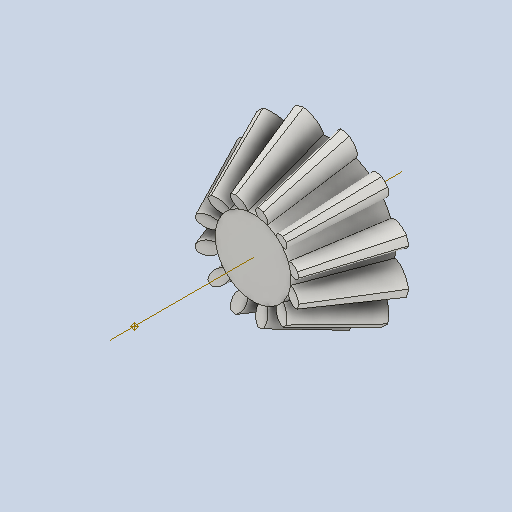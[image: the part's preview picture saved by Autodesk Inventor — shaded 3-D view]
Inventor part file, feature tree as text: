
AUTODESK INVENTOR PART (.ipt)
format: ipt  version: 2022 (Build 260153000, 153)  size: 490,496 bytes
history: native  units: mm
features: other x24, loft x2, pattern_circular x2, sketch x1
ambient origin geometry x6: Origin, XZ Plane, X Axis, Y Axis, Z Axis, Center Point
bodies: Solid1 (feature_tree)
feature tree (29):
  other  "Top Point"
  other  "Mesh Plane2"
  other  "Teeth Body"
  other  "Start Point"
  other  "Tooth Plane"
  other  "Start Sketch"
  other  "End Point"
  other  "3D Sketch Right"
  other  "End Plane Right"
  loft  "Loft Right"
  pattern_circular  "Circular Pattern Right"  [2 undecoded]
  other  "3D Sketch Left"
  other  "End Plane Left"
  loft  "Loft Left"
  pattern_circular  "Circular Pattern Left"  [2 undecoded]
  other  "Fix Body"
  other  "Mesh Plane"
  other  "Top Plane"
  other  "Teeth Body Sketch"
  other  "End Plane"
  other  "End Sketch"
  other  "Helical Curve Left"
  other  "End Sketch Left"
  other  "Body Sketch"
  sketch  "Sketch6"  dims[d0=24.0mm d1=19.543312mm d2=27.411178mm d3=12.9mm d4=29.317764mm d5=90.0deg d7=3.763947mm d8=5.032168mm d9=11.359554mm d11=13.111849mm d12=2.236532mm d15=2.990106mm d16=6.749829mm d17=0.0mm d18=90.0deg d19=0.0mm d20=90.0deg d21=120.0mm d22=360.0deg d26=153.94342mm d27=12.174046mm d28=24.0mm d29=-3.805064mm d30=2.236532mm d31=2.990106mm d32=6.749829mm d35=0.0mm d37=0.0mm d39=0.0mm d40=90.0deg d41=120.0mm d42=360.0deg d46=90.0deg d47=90.0deg d48=0.0mm d49=0.0mm d50=90.0deg d51=15.0deg d52=0.0mm d53=0.0mm d54=0.0mm d56=7.648649mm d57=16.032464mm d58=10.015958mm d59=9.526465mm d60=5.951467mm d61=9.526465mm d62=5.951467mm d63=90.0deg d64=90.0deg d65=153.94342mm d66=31.5mm d67=24.0mm d68=-3.805064mm d69=12.174046mm d70=2.990106mm d71=6.749829mm d72=2.236532mm d73=5.951467mm d74=9.526465mm d75=0.0mm d76=90.0deg d77=0.0mm d78=90.0deg d79=0.0mm d80=90.0deg d81=120.0mm d82=360.0deg d84=10.0mm d85=20.0mm d86=20.0mm d87=10.0mm d88=0.0mm d89=0.0mm]
  other  "Srf1"
  other  "Helical Curve Right"
  other  "End Sketch Right"
  other  "Pitch Diameter"
note: 4 required parameter values undecoded (feature->parameter linkage not recoverable at this tier; creation-order binding heuristic only, values carry confidence <= 0.55)
